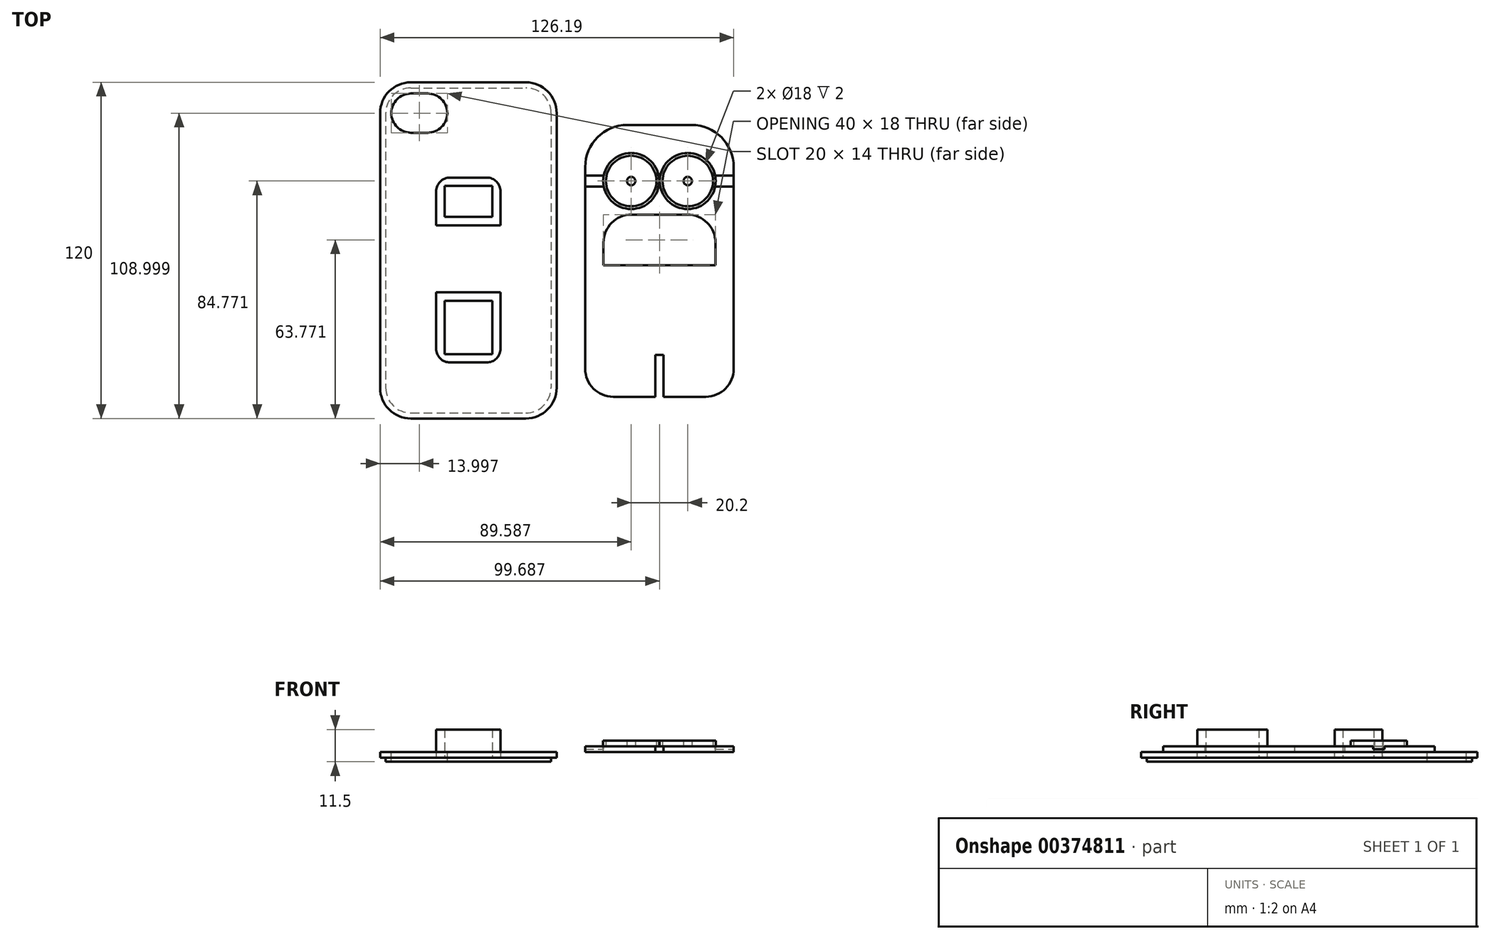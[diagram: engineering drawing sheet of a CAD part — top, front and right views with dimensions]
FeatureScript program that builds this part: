
annotation { "Feature Type Name" : "Feature", "Feature Type Description" : "" }
export const myFeature = defineFeature(function(context is Context, id is Id, definition is map)
    precondition{}
    {
        {
            var Q0;
            Q0=qCreatedBy(makeId("Top.planeOp"),FACE);
            var sketch = newSketch(context, id + "F0", { "sketchPlane" : qUnion([Q0])});
            skLineSegment(sketch, "E0.bottom", {"start": v(-23.03, 51.46) * mm, "end": v(17.97, 51.46) * mm});
            skLineSegment(sketch, "E0.top", {"start": v(-23.03, -68.54) * mm, "end": v(17.97, -68.54) * mm});
            skLineSegment(sketch, "E0.left", {"start": v(-34.03, 40.46) * mm, "end": v(-34.03, -57.54) * mm});
            skLineSegment(sketch, "E0.right", {"start": v(28.97, 40.46) * mm, "end": v(28.97, -57.54) * mm});
            skPoint(sketch, "E1.visualSharp", {"position": v(-34.03, 51.46) * mm});
            skArc(sketch, "E1.filletArc", {"start": v(-23.03, 51.46) * mm, "mid": v(-30.81, 48.24) * mm, "end": v(-34.03, 40.46) * mm});
            skPoint(sketch, "E2.visualSharp", {"position": v(28.97, 51.46) * mm});
            skArc(sketch, "E2.filletArc", {"start": v(28.97, 40.46) * mm, "mid": v(25.75, 48.24) * mm, "end": v(17.97, 51.46) * mm});
            skPoint(sketch, "E3.visualSharp", {"position": v(-34.03, -68.54) * mm});
            skArc(sketch, "E3.filletArc", {"start": v(-34.03, -57.54) * mm, "mid": v(-30.81, -65.32) * mm, "end": v(-23.03, -68.54) * mm});
            skPoint(sketch, "E4.visualSharp", {"position": v(28.97, -68.54) * mm});
            skArc(sketch, "E4.filletArc", {"start": v(17.97, -68.54) * mm, "mid": v(25.75, -65.32) * mm, "end": v(28.97, -57.54) * mm});
            skPoint(sketch, "E5.visualSharp", {"position": v(-32.03, 49.46) * mm});
            skPoint(sketch, "E6.visualSharp", {"position": v(26.97, 49.46) * mm});
            skPoint(sketch, "E7.visualSharp", {"position": v(26.97, -66.54) * mm});
            skPoint(sketch, "E8.visualSharp", {"position": v(-32.03, -66.54) * mm});
            skSolve(sketch);
        }
        {
            var Q0;
            Q0=qSketchRegion(id+"F0",true);
            extrude(context, id + "F1", {"entities" : qUnion([Q0]), "oppositeDirection" : true, "depth" : 2 * mm});
        }
        {
            var Q0;
            Q0=qCreatedBy(makeId("Top.planeOp"),FACE);
            var sketch = newSketch(context, id + "F2", { "sketchPlane" : qUnion([Q0])});
            skLineSegment(sketch, "E9.bottom", {"start": v(-23.03, 49.46) * mm, "end": v(17.97, 49.46) * mm});
            skLineSegment(sketch, "E9.top", {"start": v(-23.03, -66.54) * mm, "end": v(17.97, -66.54) * mm});
            skLineSegment(sketch, "E9.left", {"start": v(-32.03, 40.46) * mm, "end": v(-32.03, -57.54) * mm});
            skLineSegment(sketch, "E9.right", {"start": v(26.97, 40.46) * mm, "end": v(26.97, -57.54) * mm});
            skPoint(sketch, "E10.visualSharp", {"position": v(-32.03, 49.46) * mm});
            skArc(sketch, "E10.filletArc", {"start": v(-23.03, 49.46) * mm, "mid": v(-29.4, 46.82) * mm, "end": v(-32.03, 40.46) * mm});
            skPoint(sketch, "E11.visualSharp", {"position": v(26.97, 49.46) * mm});
            skArc(sketch, "E11.filletArc", {"start": v(26.97, 40.46) * mm, "mid": v(24.33, 46.82) * mm, "end": v(17.97, 49.46) * mm});
            skPoint(sketch, "E12.visualSharp", {"position": v(-32.03, -66.54) * mm});
            skArc(sketch, "E12.filletArc", {"start": v(-32.03, -57.54) * mm, "mid": v(-29.4, -63.9) * mm, "end": v(-23.03, -66.54) * mm});
            skPoint(sketch, "E13.visualSharp", {"position": v(26.97, -66.54) * mm});
            skArc(sketch, "E13.filletArc", {"start": v(17.97, -66.54) * mm, "mid": v(24.33, -63.9) * mm, "end": v(26.97, -57.54) * mm});
            skSolve(sketch);
        }
        {
            var Q0;
            Q0=qSketchRegion(id+"F2",true);
            extrude(context, id + "F3", {"entities" : qUnion([Q0]), "operationType" : NewBodyOperationType.ADD, "oppositeDirection" : true, "depth" : 3.5 * mm});
        }
        {
            var Q0;
            Q0=makeQuery(id+"F1.opExtrude","CAP_FACE",FACE,{"disambiguationData":[OSD([sQuery(id+"F0.wireOp",EDGE,"E0.bottom"),sQuery(id+"F0.wireOp",EDGE,"E0.top"),sQuery(id+"F0.wireOp",EDGE,"E0.left"),sQuery(id+"F0.wireOp",EDGE,"E0.right"),sQuery(id+"F0.wireOp",EDGE,"E1.filletArc"),sQuery(id+"F0.wireOp",EDGE,"E2.filletArc"),sQuery(id+"F0.wireOp",EDGE,"E3.filletArc"),sQuery(id+"F0.wireOp",EDGE,"E4.filletArc")])],"isStart":true});
            var sketch = newSketch(context, id + "F4", { "sketchPlane" : qUnion([Q0])});
            skLineSegment(sketch, "E14.bottom", {"start": v(-23.03, 47.46) * mm, "end": v(-17.03, 47.46) * mm});
            skLineSegment(sketch, "E14.top", {"start": v(-23.03, 33.46) * mm, "end": v(-17.03, 33.46) * mm});
            skLineSegment(sketch, "E14.left", {"start": v(-30.03, 40.46) * mm, "end": v(-30.03, 40.46) * mm});
            skLineSegment(sketch, "E14.right", {"start": v(-10.03, 40.46) * mm, "end": v(-10.03, 40.46) * mm});
            skPoint(sketch, "E15.visualSharp", {"position": v(-30.03, 47.46) * mm});
            skArc(sketch, "E15.filletArc", {"start": v(-23.03, 47.46) * mm, "mid": v(-27.98, 45.4) * mm, "end": v(-30.03, 40.46) * mm});
            skPoint(sketch, "E16.visualSharp", {"position": v(-30.03, 33.46) * mm});
            skArc(sketch, "E16.filletArc", {"start": v(-30.03, 40.46) * mm, "mid": v(-27.98, 35.5) * mm, "end": v(-23.03, 33.46) * mm});
            skPoint(sketch, "E17.visualSharp", {"position": v(-10.03, 33.46) * mm});
            skArc(sketch, "E17.filletArc", {"start": v(-17.03, 33.46) * mm, "mid": v(-12.08, 35.5) * mm, "end": v(-10.03, 40.46) * mm});
            skPoint(sketch, "E18.visualSharp", {"position": v(-10.03, 47.46) * mm});
            skArc(sketch, "E18.filletArc", {"start": v(-10.03, 40.46) * mm, "mid": v(-12.08, 45.4) * mm, "end": v(-17.03, 47.46) * mm});
            skSolve(sketch);
        }
        {
            var Q0;
            Q0=qSketchRegion(id+"F4",true);
            extrude(context, id + "F5", {"entities" : qUnion([Q0]), "operationType" : NewBodyOperationType.REMOVE, "endBound" : BoundingType.THROUGH_ALL, "oppositeDirection" : true, "depth" : 25 * mm});
        }
        {
            var Q0;
            Q0=makeQuery(id+"F1.opExtrude","CAP_FACE",FACE,{"disambiguationData":[OSD([sQuery(id+"F0.wireOp",EDGE,"E0.bottom"),sQuery(id+"F0.wireOp",EDGE,"E0.top"),sQuery(id+"F0.wireOp",EDGE,"E0.left"),sQuery(id+"F0.wireOp",EDGE,"E0.right"),sQuery(id+"F0.wireOp",EDGE,"E1.filletArc"),sQuery(id+"F0.wireOp",EDGE,"E2.filletArc"),sQuery(id+"F0.wireOp",EDGE,"E3.filletArc"),sQuery(id+"F0.wireOp",EDGE,"E4.filletArc")])],"isStart":true});
            var sketch = newSketch(context, id + "F6", { "sketchPlane" : qUnion([Q0])});
            skLineSegment(sketch, "E19.bottom", {"start": v(-9.03, 17.46) * mm, "end": v(3.97, 17.46) * mm});
            skLineSegment(sketch, "E19.top", {"start": v(-14.03, 0.46) * mm, "end": v(8.97, 0.46) * mm});
            skLineSegment(sketch, "E19.left", {"start": v(-14.03, 12.46) * mm, "end": v(-14.03, 0.46) * mm});
            skLineSegment(sketch, "E19.right", {"start": v(8.97, 12.46) * mm, "end": v(8.97, 0.46) * mm});
            skLineSegment(sketch, "E20.bottom", {"start": v(-14.03, -23.54) * mm, "end": v(8.97, -23.54) * mm});
            skLineSegment(sketch, "E20.top", {"start": v(-9.03, -48.54) * mm, "end": v(3.97, -48.54) * mm});
            skLineSegment(sketch, "E20.left", {"start": v(-14.03, -23.54) * mm, "end": v(-14.03, -43.54) * mm});
            skLineSegment(sketch, "E20.right", {"start": v(8.97, -23.54) * mm, "end": v(8.97, -43.54) * mm});
            skPoint(sketch, "E21.visualSharp", {"position": v(-14.03, -48.54) * mm});
            skArc(sketch, "E21.filletArc", {"start": v(-14.03, -43.54) * mm, "mid": v(-12.57, -47.08) * mm, "end": v(-9.03, -48.54) * mm});
            skPoint(sketch, "E22.visualSharp", {"position": v(8.97, -48.54) * mm});
            skArc(sketch, "E22.filletArc", {"start": v(3.97, -48.54) * mm, "mid": v(7.5, -47.08) * mm, "end": v(8.97, -43.54) * mm});
            skPoint(sketch, "E23.visualSharp", {"position": v(-14.03, 17.46) * mm});
            skArc(sketch, "E23.filletArc", {"start": v(-9.03, 17.46) * mm, "mid": v(-12.57, 16) * mm, "end": v(-14.03, 12.46) * mm});
            skPoint(sketch, "E24.visualSharp", {"position": v(8.97, 17.46) * mm});
            skArc(sketch, "E24.filletArc", {"start": v(8.97, 12.46) * mm, "mid": v(7.5, 16) * mm, "end": v(3.97, 17.46) * mm});
            skSolve(sketch);
        }
        {
            var Q0;
            Q0=qSketchRegion(id+"F6",true);
            extrude(context, id + "F7", {"entities" : qUnion([Q0]), "operationType" : NewBodyOperationType.REMOVE, "oppositeDirection" : true, "depth" : 2 * mm});
        }
        {
            var Q0;
            Q0=makeQuery(id+"F7.boolean.opBoolean","COPY",FACE,{"derivedFrom":makeQuery(id+"F7.opExtrude","CAP_FACE",FACE,{"disambiguationData":[OSD([sQuery(id+"F6.wireOp",EDGE,"E19.bottom"),sQuery(id+"F6.wireOp",EDGE,"E19.top"),sQuery(id+"F6.wireOp",EDGE,"E19.left"),sQuery(id+"F6.wireOp",EDGE,"E19.right"),sQuery(id+"F6.wireOp",EDGE,"E23.filletArc"),sQuery(id+"F6.wireOp",EDGE,"E24.filletArc")])],"isStart":false})});
            var sketch = newSketch(context, id + "F8", { "sketchPlane" : qUnion([Q0])});
            skPoint(sketch, "E25.visualSharp", {"position": v(8.97, 17.46) * mm});
            skPoint(sketch, "E26.visualSharp", {"position": v(-14.03, -48.54) * mm});
            skArc(sketch, "E27.filletArc", {"start": v(3.97, -48.54) * mm, "mid": v(7.5, -47.08) * mm, "end": v(8.97, -43.54) * mm});
            skLineSegment(sketch, "E28.top", {"start": v(-14.03, 0.46) * mm, "end": v(8.97, 0.46) * mm});
            skLineSegment(sketch, "E29.bottom", {"start": v(-14.03, -23.54) * mm, "end": v(8.97, -23.54) * mm});
            skLineSegment(sketch, "E28.left", {"start": v(-14.03, 12.46) * mm, "end": v(-14.03, 0.46) * mm});
            skArc(sketch, "E25.filletArc", {"start": v(8.97, 12.46) * mm, "mid": v(7.5, 16) * mm, "end": v(3.97, 17.46) * mm});
            skArc(sketch, "E30.filletArc", {"start": v(-9.03, 17.46) * mm, "mid": v(-12.57, 16) * mm, "end": v(-14.03, 12.46) * mm});
            skPoint(sketch, "E30.visualSharp", {"position": v(-14.03, 17.46) * mm});
            skPoint(sketch, "E27.visualSharp", {"position": v(8.97, -48.54) * mm});
            skLineSegment(sketch, "E29.right", {"start": v(8.97, -23.54) * mm, "end": v(8.97, -43.54) * mm});
            skLineSegment(sketch, "E29.left", {"start": v(-14.03, -23.54) * mm, "end": v(-14.03, -43.54) * mm});
            skLineSegment(sketch, "E28.bottom", {"start": v(-9.03, 17.46) * mm, "end": v(3.97, 17.46) * mm});
            skLineSegment(sketch, "E28.right", {"start": v(8.97, 12.46) * mm, "end": v(8.97, 0.46) * mm});
            skLineSegment(sketch, "E29.top", {"start": v(-9.03, -48.54) * mm, "end": v(3.97, -48.54) * mm});
            skArc(sketch, "E26.filletArc", {"start": v(-14.03, -43.54) * mm, "mid": v(-12.57, -47.08) * mm, "end": v(-9.03, -48.54) * mm});
            skLineSegment(sketch, "E31.bottom", {"start": v(-11.03, 14.46) * mm, "end": v(5.97, 14.46) * mm});
            skLineSegment(sketch, "E31.top", {"start": v(-11.03, 3.46) * mm, "end": v(5.97, 3.46) * mm});
            skLineSegment(sketch, "E31.left", {"start": v(-11.03, 14.46) * mm, "end": v(-11.03, 3.46) * mm});
            skLineSegment(sketch, "E31.right", {"start": v(5.97, 14.46) * mm, "end": v(5.97, 3.46) * mm});
            skLineSegment(sketch, "E32.bottom", {"start": v(-11.03, -26.54) * mm, "end": v(5.97, -26.54) * mm});
            skLineSegment(sketch, "E32.top", {"start": v(-11.03, -45.54) * mm, "end": v(5.97, -45.54) * mm});
            skLineSegment(sketch, "E32.left", {"start": v(-11.03, -26.54) * mm, "end": v(-11.03, -45.54) * mm});
            skLineSegment(sketch, "E32.right", {"start": v(5.97, -26.54) * mm, "end": v(5.97, -45.54) * mm});
            skSolve(sketch);
        }
        {
            var Q0;
            Q0=qSketchRegion(id+"F8",true);
            extrude(context, id + "F9", {"entities" : qUnion([Q0]), "depth" : 10 * mm});
        }
        {
            var Q0;
            Q0=qCreatedBy(makeId("Top.planeOp"),FACE);
            var sketch = newSketch(context, id + "F10", { "sketchPlane" : qUnion([Q0])});
            skLineSegment(sketch, "E33.bottom", {"start": v(54.16, 36.23) * mm, "end": v(77.16, 36.23) * mm});
            skLineSegment(sketch, "E33.top", {"start": v(49.16, -60.77) * mm, "end": v(82.16, -60.77) * mm});
            skLineSegment(sketch, "E33.left", {"start": v(39.16, 21.23) * mm, "end": v(39.16, -50.77) * mm});
            skLineSegment(sketch, "E33.right", {"start": v(92.16, 21.23) * mm, "end": v(92.16, -50.77) * mm});
            skPoint(sketch, "E34.visualSharp", {"position": v(39.16, 36.23) * mm});
            skArc(sketch, "E34.filletArc", {"start": v(54.16, 36.23) * mm, "mid": v(43.55, 31.84) * mm, "end": v(39.16, 21.23) * mm});
            skPoint(sketch, "E35.visualSharp", {"position": v(92.16, 36.23) * mm});
            skArc(sketch, "E35.filletArc", {"start": v(92.16, 21.23) * mm, "mid": v(87.76, 31.84) * mm, "end": v(77.16, 36.23) * mm});
            skPoint(sketch, "E36.visualSharp", {"position": v(39.16, -60.77) * mm});
            skArc(sketch, "E36.filletArc", {"start": v(39.16, -50.77) * mm, "mid": v(42.09, -57.84) * mm, "end": v(49.16, -60.77) * mm});
            skPoint(sketch, "E37.visualSharp", {"position": v(92.16, -60.77) * mm});
            skArc(sketch, "E37.filletArc", {"start": v(82.16, -60.77) * mm, "mid": v(89.23, -57.84) * mm, "end": v(92.16, -50.77) * mm});
            skSolve(sketch);
        }
        {
            var Q0;
            Q0=qSketchRegion(id+"F10",true);
            extrude(context, id + "F11", {"entities" : qUnion([Q0]), "depth" : 2 * mm});
        }
        {
            var Q0;
            Q0=makeQuery(id+"F11.opExtrude","CAP_FACE",FACE,{"disambiguationData":[OSD([sQuery(id+"F10.wireOp",EDGE,"E33.bottom"),sQuery(id+"F10.wireOp",EDGE,"E33.top"),sQuery(id+"F10.wireOp",EDGE,"E33.left"),sQuery(id+"F10.wireOp",EDGE,"E33.right"),sQuery(id+"F10.wireOp",EDGE,"E34.filletArc"),sQuery(id+"F10.wireOp",EDGE,"E35.filletArc"),sQuery(id+"F10.wireOp",EDGE,"E36.filletArc"),sQuery(id+"F10.wireOp",EDGE,"E37.filletArc")])],"isStart":false});
            var sketch = newSketch(context, id + "F12", { "sketchPlane" : qUnion([Q0])});
            skLineSegment(sketch, "E38.bottom", {"start": v(55.66, 4.23) * mm, "end": v(75.66, 4.23) * mm});
            skLineSegment(sketch, "E38.top", {"start": v(45.66, -13.77) * mm, "end": v(85.66, -13.77) * mm});
            skLineSegment(sketch, "E38.left", {"start": v(85.66, -5.77) * mm, "end": v(85.66, -13.77) * mm});
            skLineSegment(sketch, "E38.right", {"start": v(45.66, -5.77) * mm, "end": v(45.66, -13.77) * mm});
            skLineSegment(sketch, "E39.bottom", {"start": v(67.16, -45.77) * mm, "end": v(64.16, -45.77) * mm});
            skLineSegment(sketch, "E39.top", {"start": v(67.16, -60.77) * mm, "end": v(64.16, -60.77) * mm});
            skLineSegment(sketch, "E39.left", {"start": v(64.16, -45.77) * mm, "end": v(64.16, -60.77) * mm});
            skLineSegment(sketch, "E39.right", {"start": v(67.16, -45.77) * mm, "end": v(67.16, -60.77) * mm});
            skPoint(sketch, "E40.visualSharp", {"position": v(45.66, 4.23) * mm});
            skArc(sketch, "E40.filletArc", {"start": v(55.66, 4.23) * mm, "mid": v(48.59, 1.3) * mm, "end": v(45.66, -5.77) * mm});
            skPoint(sketch, "E41.visualSharp", {"position": v(85.66, 4.23) * mm});
            skArc(sketch, "E41.filletArc", {"start": v(85.66, -5.77) * mm, "mid": v(82.73, 1.3) * mm, "end": v(75.66, 4.23) * mm});
            skSolve(sketch);
        }
        {
            var Q0;
            Q0=qSketchRegion(id+"F12",true);
            extrude(context, id + "F13", {"entities" : qUnion([Q0]), "operationType" : NewBodyOperationType.REMOVE, "endBound" : BoundingType.THROUGH_ALL, "oppositeDirection" : true, "depth" : 25 * mm});
        }
        {
            var Q0;
            Q0=makeQuery(id+"F11.opExtrude","CAP_FACE",FACE,{"disambiguationData":[OSD([sQuery(id+"F10.wireOp",EDGE,"E33.bottom"),sQuery(id+"F10.wireOp",EDGE,"E33.top"),sQuery(id+"F10.wireOp",EDGE,"E33.left"),sQuery(id+"F10.wireOp",EDGE,"E33.right"),sQuery(id+"F10.wireOp",EDGE,"E34.filletArc"),sQuery(id+"F10.wireOp",EDGE,"E35.filletArc"),sQuery(id+"F10.wireOp",EDGE,"E36.filletArc"),sQuery(id+"F10.wireOp",EDGE,"E37.filletArc")])],"isStart":false});
            var sketch = newSketch(context, id + "F14", { "sketchPlane" : qUnion([Q0])});
            skLineSegment(sketch, "E42.bottom", {"start": v(39.16, 18.23) * mm, "end": v(45.76, 18.23) * mm});
            skLineSegment(sketch, "E42.top", {"start": v(39.16, 14.23) * mm, "end": v(45.76, 14.23) * mm});
            skLineSegment(sketch, "E42.left", {"start": v(39.16, 18.23) * mm, "end": v(39.16, 14.23) * mm});
            skLineSegment(sketch, "E43.bottom", {"start": v(85.56, 18.23) * mm, "end": v(92.16, 18.23) * mm});
            skLineSegment(sketch, "E43.top", {"start": v(85.56, 14.23) * mm, "end": v(92.16, 14.23) * mm});
            skLineSegment(sketch, "E43.right", {"start": v(92.16, 18.23) * mm, "end": v(92.16, 14.23) * mm});
            skArc(sketch, "E44", {"start": v(45.76, 18.23) * mm, "mid": v(45.56, 16.23) * mm, "end": v(45.76, 14.23) * mm});
            skArc(sketch, "E45", {"start": v(85.56, 14.23) * mm, "mid": v(85.76, 16.23) * mm, "end": v(85.56, 18.23) * mm});
            skSolve(sketch);
        }
        {
            var Q0;
            Q0=makeQuery(id+"F14.imprint","IMPRINT",FACE,{"disambiguationData":[TD([[makeQuery(id+"F14.imprint","IMPRINT",EDGE,{"derivedFrom":sQuery(id+"F14.wireOp",EDGE,"E42.bottom")}),-1.0]])]});
            var Q1;
            Q1=makeQuery(id+"F14.imprint","IMPRINT",FACE,{"disambiguationData":[TD([[makeQuery(id+"F14.imprint","IMPRINT",EDGE,{"derivedFrom":sQuery(id+"F14.wireOp",EDGE,"E43.bottom")}),-1.0]])]});
            extrude(context, id + "F15", {"entities" : qUnion([Q0, Q1]), "operationType" : NewBodyOperationType.REMOVE, "oppositeDirection" : true, "depth" : 1 * mm});
        }
        {
            var Q0;
            Q0=makeQuery(id+"F11.opExtrude","CAP_FACE",FACE,{"disambiguationData":[OSD([sQuery(id+"F10.wireOp",EDGE,"E33.bottom"),sQuery(id+"F10.wireOp",EDGE,"E33.top"),sQuery(id+"F10.wireOp",EDGE,"E33.left"),sQuery(id+"F10.wireOp",EDGE,"E33.right"),sQuery(id+"F10.wireOp",EDGE,"E34.filletArc"),sQuery(id+"F10.wireOp",EDGE,"E35.filletArc"),sQuery(id+"F10.wireOp",EDGE,"E36.filletArc"),sQuery(id+"F10.wireOp",EDGE,"E37.filletArc")])],"isStart":false});
            var sketch = newSketch(context, id + "F16", { "sketchPlane" : qUnion([Q0])});
            skCircle(sketch, "E46", {"center": v(55.56, 16.23) * mm, "radius": 10 * mm});
            skCircle(sketch, "E47", {"center": v(55.56, 16.23) * mm, "radius": 9 * mm});
            skCircle(sketch, "E48", {"center": v(75.76, 16.23) * mm, "radius": 10 * mm});
            skCircle(sketch, "E49", {"center": v(75.76, 16.23) * mm, "radius": 9 * mm});
            skCircle(sketch, "E50", {"center": v(55.56, 16.23) * mm, "radius": 1.5 * mm});
            skCircle(sketch, "E51", {"center": v(75.76, 16.23) * mm, "radius": 1.5 * mm});
            skSolve(sketch);
        }
        {
            var Q0;
            Q0=qSketchRegion(id+"F16",true);
            var Q1;
            Q1=makeQuery(id+"F16.imprint","IMPRINT",FACE,{"disambiguationData":[TD([[makeQuery(id+"F16.imprint","IMPRINT",EDGE,{"derivedFrom":sQuery(id+"F16.wireOp",EDGE,"E50")}),1.0]])]});
            var Q2;
            Q2=makeQuery(id+"F16.imprint","IMPRINT",FACE,{"disambiguationData":[TD([[makeQuery(id+"F16.imprint","IMPRINT",EDGE,{"derivedFrom":sQuery(id+"F16.wireOp",EDGE,"E51")}),1.0]])]});
            extrude(context, id + "F17", {"entities" : qUnion([Q0, Q1, Q2]), "operationType" : NewBodyOperationType.ADD, "depth" : 2 * mm});
        }
    });
